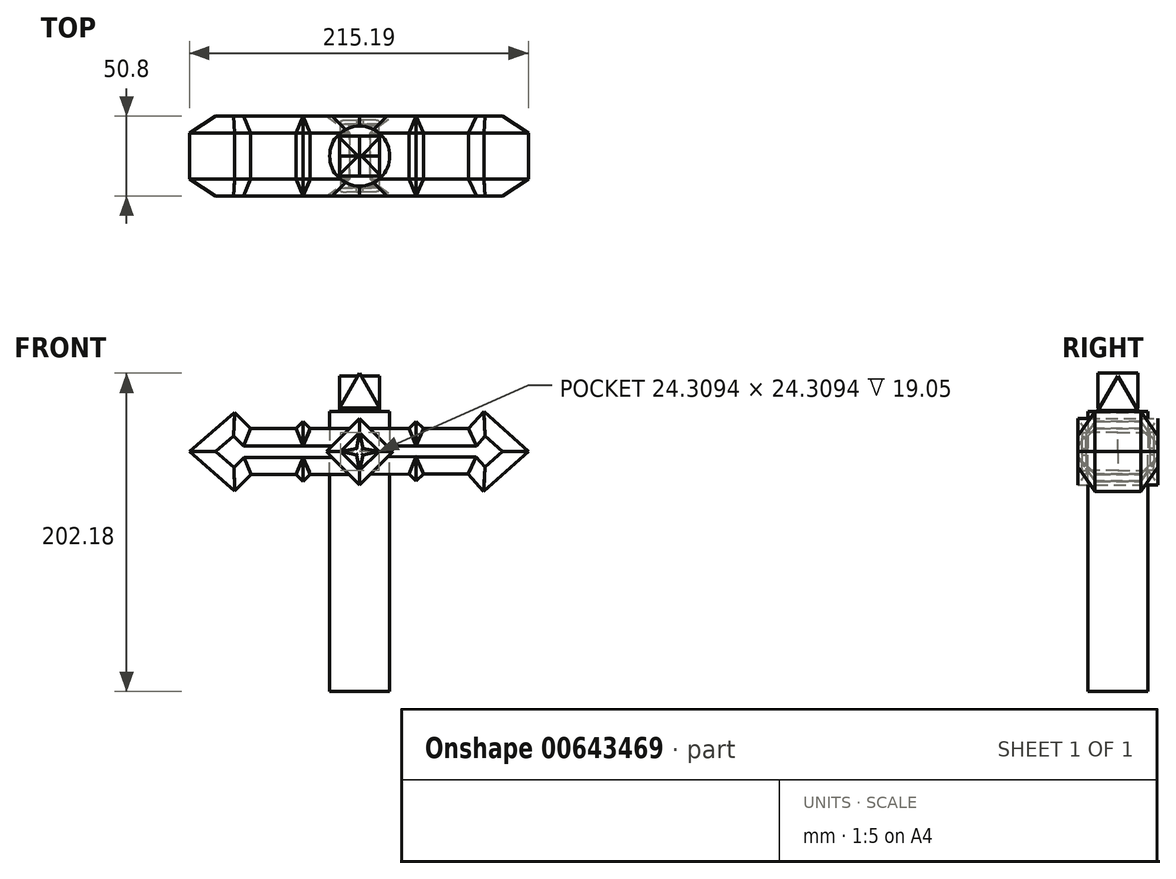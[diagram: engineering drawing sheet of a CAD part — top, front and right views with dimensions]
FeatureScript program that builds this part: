
annotation { "Feature Type Name" : "Feature", "Feature Type Description" : "" }
export const myFeature = defineFeature(function(context is Context, id is Id, definition is map)
    precondition{}
    {
        {
            var Q0;
            Q0=qCreatedBy(makeId("Front.planeOp"),FACE);
            var sketch = newSketch(context, id + "F0", { "sketchPlane" : qUnion([Q0])});
            skLineSegment(sketch, "E0", {"start": v(-21.13, 0) * mm, "end": v(0, 21.13) * mm});
            skLineSegment(sketch, "E1", {"start": v(0, 21.13) * mm, "end": v(21.13, 0) * mm});
            skLineSegment(sketch, "E2", {"start": v(21.13, 0) * mm, "end": v(0, -21.13) * mm});
            skLineSegment(sketch, "E3", {"start": v(0, -21.13) * mm, "end": v(-21.13, 0) * mm});
            skLineSegment(sketch, "E4", {"start": v(-6.56, 14.57) * mm, "end": v(-31.36, 14.57) * mm});
            skLineSegment(sketch, "E5", {"start": v(-31.36, 14.57) * mm, "end": v(-35.9, 19.12) * mm});
            skLineSegment(sketch, "E6", {"start": v(-35.9, 19.12) * mm, "end": v(-40.45, 14.57) * mm});
            skLineSegment(sketch, "E7", {"start": v(-40.45, 14.57) * mm, "end": v(-69.24, 14.57) * mm});
            skLineSegment(sketch, "E8", {"start": v(-69.24, 14.57) * mm, "end": v(-79.35, 24.94) * mm});
            skLineSegment(sketch, "E9", {"start": v(-79.35, 24.94) * mm, "end": v(-108.04, 0) * mm});
            skLineSegment(sketch, "E10", {"start": v(-6.56, -14.57) * mm, "end": v(-31.36, -14.57) * mm});
            skLineSegment(sketch, "E11", {"start": v(-31.36, -14.57) * mm, "end": v(-35.9, -19.12) * mm});
            skLineSegment(sketch, "E12", {"start": v(-35.9, -19.12) * mm, "end": v(-40.45, -14.57) * mm});
            skLineSegment(sketch, "E13", {"start": v(-40.45, -14.57) * mm, "end": v(-68.98, -14.57) * mm});
            skLineSegment(sketch, "E14", {"start": v(-68.98, -14.57) * mm, "end": v(-79.35, -24.94) * mm});
            skLineSegment(sketch, "E15", {"start": v(-79.35, -24.94) * mm, "end": v(-108.04, 0) * mm});
            skLineSegment(sketch, "E16", {"start": v(6.56, 14.57) * mm, "end": v(31.35, 14.57) * mm});
            skLineSegment(sketch, "E17", {"start": v(31.35, 14.57) * mm, "end": v(35.9, 19.11) * mm});
            skLineSegment(sketch, "E18", {"start": v(35.9, 19.11) * mm, "end": v(40.44, 14.57) * mm});
            skLineSegment(sketch, "E19", {"start": v(40.44, 14.57) * mm, "end": v(69.23, 14.57) * mm});
            skLineSegment(sketch, "E20", {"start": v(69.23, 14.57) * mm, "end": v(78.85, 25.4) * mm});
            skLineSegment(sketch, "E21", {"start": v(78.85, 25.4) * mm, "end": v(107.15, 0) * mm});
            skLineSegment(sketch, "E22", {"start": v(107.15, 0) * mm, "end": v(78.7, -25.22) * mm});
            skLineSegment(sketch, "E23", {"start": v(78.7, -25.22) * mm, "end": v(68.97, -14.24) * mm});
            skLineSegment(sketch, "E24", {"start": v(68.97, -14.24) * mm, "end": v(40.44, -14.24) * mm});
            skLineSegment(sketch, "E25", {"start": v(40.44, -14.24) * mm, "end": v(35.9, -18.79) * mm});
            skLineSegment(sketch, "E26", {"start": v(35.9, -18.79) * mm, "end": v(31.35, -14.24) * mm});
            skLineSegment(sketch, "E27", {"start": v(31.35, -14.24) * mm, "end": v(6.56, -14.57) * mm});
            skLineSegment(sketch, "E28.0", {"start": v(0, 12.15) * mm, "end": v(12.15, 0) * mm});
            skLineSegment(sketch, "E28.1", {"start": v(-12.15, 0) * mm, "end": v(0, 12.15) * mm});
            skLineSegment(sketch, "E28.2", {"start": v(0, -12.15) * mm, "end": v(-12.15, 0) * mm});
            skLineSegment(sketch, "E28.3", {"start": v(12.15, 0) * mm, "end": v(0, -12.15) * mm});
            skLineSegment(sketch, "E29", {"start": v(0, 12.15) * mm, "end": v(-2.1, 2.07) * mm});
            skLineSegment(sketch, "E30", {"start": v(-2.1, 2.07) * mm, "end": v(-12.15, 0) * mm});
            skLineSegment(sketch, "E31", {"start": v(-12.15, 0) * mm, "end": v(-2.1, -2.1) * mm});
            skLineSegment(sketch, "E32", {"start": v(-2.1, -2.1) * mm, "end": v(0, -12.15) * mm});
            skLineSegment(sketch, "E33", {"start": v(1.98, -2.1) * mm, "end": v(0, -12.15) * mm});
            skLineSegment(sketch, "E34", {"start": v(12.15, 0) * mm, "end": v(1.98, -2.1) * mm});
            skLineSegment(sketch, "E35", {"start": v(12.15, 0) * mm, "end": v(1.98, 2) * mm});
            skLineSegment(sketch, "E36", {"start": v(1.98, 2) * mm, "end": v(0, 12.15) * mm});
            skLineSegment(sketch, "E37", {"start": v(31.35, 14.57) * mm, "end": v(31.35, -14.24) * mm});
            skLineSegment(sketch, "E38", {"start": v(40.44, 14.57) * mm, "end": v(40.44, -14.24) * mm});
            skLineSegment(sketch, "E39", {"start": v(-31.36, 14.57) * mm, "end": v(-31.36, -14.57) * mm});
            skLineSegment(sketch, "E40", {"start": v(-40.45, -14.57) * mm, "end": v(-40.45, 14.57) * mm});
            skLineSegment(sketch, "E41", {"start": v(78.85, 25.4) * mm, "end": v(78.7, -25.22) * mm});
            skLineSegment(sketch, "E42", {"start": v(-79.35, 24.94) * mm, "end": v(-79.35, -24.94) * mm});
            skLineSegment(sketch, "E43", {"start": v(69.23, 14.57) * mm, "end": v(68.97, -14.24) * mm});
            skLineSegment(sketch, "E44", {"start": v(-69.24, 14.57) * mm, "end": v(-68.98, -14.57) * mm});
            skLineSegment(sketch, "E45", {"start": v(107.15, 0) * mm, "end": v(78.7, 0) * mm});
            skLineSegment(sketch, "E46", {"start": v(-108.04, 0) * mm, "end": v(-79.35, 0) * mm});
            skLineSegment(sketch, "E47", {"start": v(-79.35, 0) * mm, "end": v(-21.13, 0) * mm});
            skLineSegment(sketch, "E48", {"start": v(78.7, 0) * mm, "end": v(21.13, 0) * mm});
            skSolve(sketch);
        }
        {
            var Q0;
            {var subQ0=sQuery(id+"F0.wireOp",EDGE,"E15");Q0=makeQuery(id+"F0.imprint","IMPRINT",FACE,{"disambiguationData":[TD([[makeQuery(id+"F0.imprint","IMPRINT",EDGE,{"derivedFrom":subQ0}),-1.0]])]});}
            var Q1;
            {var subQ0=sQuery(id+"F0.wireOp",EDGE,"E9");Q1=makeQuery(id+"F0.imprint","IMPRINT",FACE,{"disambiguationData":[TD([[makeQuery(id+"F0.imprint","IMPRINT",EDGE,{"derivedFrom":subQ0}),1.0]])]});}
            var Q2;
            {var subQ0=sQuery(id+"F0.wireOp",EDGE,"E8");Q2=makeQuery(id+"F0.imprint","IMPRINT",FACE,{"disambiguationData":[TD([[makeQuery(id+"F0.imprint","IMPRINT",EDGE,{"derivedFrom":subQ0}),1.0]])]});}
            var Q3;
            {var subQ0=sQuery(id+"F0.wireOp",EDGE,"E14");Q3=makeQuery(id+"F0.imprint","IMPRINT",FACE,{"disambiguationData":[TD([[makeQuery(id+"F0.imprint","IMPRINT",EDGE,{"derivedFrom":subQ0}),-1.0]])]});}
            var Q4;
            {var subQ0=sQuery(id+"F0.wireOp",EDGE,"E13");Q4=makeQuery(id+"F0.imprint","IMPRINT",FACE,{"disambiguationData":[TD([[makeQuery(id+"F0.imprint","IMPRINT",EDGE,{"derivedFrom":subQ0}),-1.0]])]});}
            var Q5;
            {var subQ0=sQuery(id+"F0.wireOp",EDGE,"E7");Q5=makeQuery(id+"F0.imprint","IMPRINT",FACE,{"disambiguationData":[TD([[makeQuery(id+"F0.imprint","IMPRINT",EDGE,{"derivedFrom":subQ0}),1.0]])]});}
            var Q6;
            {var subQ5=sQuery(id+"F0.wireOp",EDGE,"E5");Q6=makeQuery(id+"F0.imprint","IMPRINT",FACE,{"disambiguationData":[TD([[makeQuery(id+"F0.imprint","IMPRINT",EDGE,{"derivedFrom":subQ5}),1.0]])]});}
            var Q7;
            {var subQ1=sQuery(id+"F0.wireOp",EDGE,"E11");Q7=makeQuery(id+"F0.imprint","IMPRINT",FACE,{"disambiguationData":[TD([[makeQuery(id+"F0.imprint","IMPRINT",EDGE,{"derivedFrom":subQ1}),-1.0]])]});}
            extrude(context, id + "F1", {"entities" : qUnion([Q0, Q1, Q2, Q3, Q4, Q5, Q6, Q7]), "depth" : 25.4 * mm, "offsetDistance" : 25.4 * mm});
        }
        {
            var Q0;
            {var subQ3=sQuery(id+"F0.wireOp",EDGE,"E4");Q0=makeQuery(id+"F0.imprint","IMPRINT",FACE,{"disambiguationData":[TD([[makeQuery(id+"F0.imprint","IMPRINT",EDGE,{"derivedFrom":subQ3}),1.0]])]});}
            var Q1;
            {var subQ3=sQuery(id+"F0.wireOp",EDGE,"E10");Q1=makeQuery(id+"F0.imprint","IMPRINT",FACE,{"disambiguationData":[TD([[makeQuery(id+"F0.imprint","IMPRINT",EDGE,{"derivedFrom":subQ3}),-1.0]])]});}
            var Q2;
            Q2=makeQuery(id+"F0.imprint","IMPRINT",FACE,{"disambiguationData":[TD([[makeQuery(id+"F0.imprint","IMPRINT",EDGE,{"derivedFrom":sQuery(id+"F0.wireOp",EDGE,"E28.0")}),1.0]])]});
            var Q3;
            {var subQ3=sQuery(id+"F0.wireOp",EDGE,"E27");Q3=makeQuery(id+"F0.imprint","IMPRINT",FACE,{"disambiguationData":[TD([[makeQuery(id+"F0.imprint","IMPRINT",EDGE,{"derivedFrom":subQ3}),-1.0]])]});}
            var Q4;
            {var subQ3=sQuery(id+"F0.wireOp",EDGE,"E16");Q4=makeQuery(id+"F0.imprint","IMPRINT",FACE,{"disambiguationData":[TD([[makeQuery(id+"F0.imprint","IMPRINT",EDGE,{"derivedFrom":subQ3}),-1.0]])]});}
            var Q5;
            {var subQ1=sQuery(id+"F0.wireOp",EDGE,"E17");Q5=makeQuery(id+"F0.imprint","IMPRINT",FACE,{"disambiguationData":[TD([[makeQuery(id+"F0.imprint","IMPRINT",EDGE,{"derivedFrom":subQ1}),-1.0]])]});}
            var Q6;
            {var subQ0=sQuery(id+"F0.wireOp",EDGE,"E19");Q6=makeQuery(id+"F0.imprint","IMPRINT",FACE,{"disambiguationData":[TD([[makeQuery(id+"F0.imprint","IMPRINT",EDGE,{"derivedFrom":subQ0}),-1.0]])]});}
            var Q7;
            {var subQ1=sQuery(id+"F0.wireOp",EDGE,"E25");Q7=makeQuery(id+"F0.imprint","IMPRINT",FACE,{"disambiguationData":[TD([[makeQuery(id+"F0.imprint","IMPRINT",EDGE,{"derivedFrom":subQ1}),-1.0]])]});}
            var Q8;
            {var subQ0=sQuery(id+"F0.wireOp",EDGE,"E24");Q8=makeQuery(id+"F0.imprint","IMPRINT",FACE,{"disambiguationData":[TD([[makeQuery(id+"F0.imprint","IMPRINT",EDGE,{"derivedFrom":subQ0}),-1.0]])]});}
            var Q9;
            {var subQ5=sQuery(id+"F0.wireOp",EDGE,"E23");Q9=makeQuery(id+"F0.imprint","IMPRINT",FACE,{"disambiguationData":[TD([[makeQuery(id+"F0.imprint","IMPRINT",EDGE,{"derivedFrom":subQ5}),-1.0]])]});}
            var Q10;
            {var subQ6=sQuery(id+"F0.wireOp",EDGE,"E20");Q10=makeQuery(id+"F0.imprint","IMPRINT",FACE,{"disambiguationData":[TD([[makeQuery(id+"F0.imprint","IMPRINT",EDGE,{"derivedFrom":subQ6}),-1.0]])]});}
            var Q11;
            {var subQ0=sQuery(id+"F0.wireOp",EDGE,"E21");Q11=makeQuery(id+"F0.imprint","IMPRINT",FACE,{"disambiguationData":[TD([[makeQuery(id+"F0.imprint","IMPRINT",EDGE,{"derivedFrom":subQ0}),-1.0]])]});}
            var Q12;
            {var subQ0=sQuery(id+"F0.wireOp",EDGE,"E22");Q12=makeQuery(id+"F0.imprint","IMPRINT",FACE,{"disambiguationData":[TD([[makeQuery(id+"F0.imprint","IMPRINT",EDGE,{"derivedFrom":subQ0}),-1.0]])]});}
            extrude(context, id + "F2", {"entities" : qUnion([Q0, Q1, Q2, Q3, Q4, Q5, Q6, Q7, Q8, Q9, Q10, Q11, Q12]), "operationType" : NewBodyOperationType.ADD, "depth" : 25.4 * mm, "offsetDistance" : 25.4 * mm});
        }
        {
            var Q0;
            Q0=makeQuery(id+"F2.opExtrude","CAP_EDGE",EDGE,{"disambiguationData":[OSD([sQuery(id+"F0.wireOp",EDGE,"E28.1")])],"isStart":false});
            var Q1;
            Q1=makeQuery(id+"F2.opExtrude","CAP_EDGE",EDGE,{"disambiguationData":[OSD([sQuery(id+"F0.wireOp",EDGE,"E28.0")])],"isStart":false});
            var Q2;
            Q2=makeQuery(id+"F2.opExtrude","CAP_EDGE",EDGE,{"disambiguationData":[OSD([sQuery(id+"F0.wireOp",EDGE,"E28.3")])],"isStart":false});
            var Q3;
            Q3=makeQuery(id+"F2.opExtrude","CAP_EDGE",EDGE,{"disambiguationData":[OSD([sQuery(id+"F0.wireOp",EDGE,"E28.2")])],"isStart":false});
            chamfer(context, id + "F3", {"entities" : qUnion([Q0, Q1, Q2, Q3]), "width" : 6.35 * mm, "tangentPropagation" : true});
        }
        {
            var Q0;
            Q0=makeQuery(id+"F0.imprint","IMPRINT",FACE,{"disambiguationData":[TD([[makeQuery(id+"F0.imprint","IMPRINT",EDGE,{"derivedFrom":sQuery(id+"F0.wireOp",EDGE,"E29")}),1.0]])]});
            extrude(context, id + "F4", {"entities" : qUnion([Q0]), "depth" : 22.86 * mm, "offsetDistance" : 25.4 * mm});
        }
        {
            var Q0;
            Q0=makeQuery(id+"F0.imprint","IMPRINT",FACE,{"disambiguationData":[TD([[makeQuery(id+"F0.imprint","IMPRINT",EDGE,{"derivedFrom":sQuery(id+"F0.wireOp",EDGE,"E28.0")}),-1.0]])]});
            var Q1;
            Q1=makeQuery(id+"F0.imprint","IMPRINT",FACE,{"disambiguationData":[TD([[makeQuery(id+"F0.imprint","IMPRINT",EDGE,{"derivedFrom":sQuery(id+"F0.wireOp",EDGE,"E28.3")}),-1.0]])]});
            var Q2;
            Q2=makeQuery(id+"F0.imprint","IMPRINT",FACE,{"disambiguationData":[TD([[makeQuery(id+"F0.imprint","IMPRINT",EDGE,{"derivedFrom":sQuery(id+"F0.wireOp",EDGE,"E28.2")}),-1.0]])]});
            var Q3;
            Q3=makeQuery(id+"F0.imprint","IMPRINT",FACE,{"disambiguationData":[TD([[makeQuery(id+"F0.imprint","IMPRINT",EDGE,{"derivedFrom":sQuery(id+"F0.wireOp",EDGE,"E28.1")}),-1.0]])]});
            extrude(context, id + "F5", {"entities" : qUnion([Q0, Q1, Q2, Q3]), "depth" : 20.32 * mm, "offsetDistance" : 25.4 * mm});
        }
        {
            var Q0;
            Q0=makeQuery(id+"F4.opExtrude","CAP_EDGE",EDGE,{"disambiguationData":[OSD([sQuery(id+"F0.wireOp",EDGE,"E35")])],"isStart":false});
            var Q1;
            Q1=makeQuery(id+"F4.opExtrude","CAP_EDGE",EDGE,{"disambiguationData":[OSD([sQuery(id+"F0.wireOp",EDGE,"E34")])],"isStart":false});
            var Q2;
            Q2=makeQuery(id+"F4.opExtrude","CAP_EDGE",EDGE,{"disambiguationData":[OSD([sQuery(id+"F0.wireOp",EDGE,"E33")])],"isStart":false});
            var Q3;
            Q3=makeQuery(id+"F4.opExtrude","CAP_EDGE",EDGE,{"disambiguationData":[OSD([sQuery(id+"F0.wireOp",EDGE,"E32")])],"isStart":false});
            var Q4;
            Q4=makeQuery(id+"F4.opExtrude","CAP_EDGE",EDGE,{"disambiguationData":[OSD([sQuery(id+"F0.wireOp",EDGE,"E31")])],"isStart":false});
            var Q5;
            Q5=makeQuery(id+"F4.opExtrude","CAP_EDGE",EDGE,{"disambiguationData":[OSD([sQuery(id+"F0.wireOp",EDGE,"E30")])],"isStart":false});
            var Q6;
            Q6=makeQuery(id+"F4.opExtrude","CAP_EDGE",EDGE,{"disambiguationData":[OSD([sQuery(id+"F0.wireOp",EDGE,"E29")])],"isStart":false});
            var Q7;
            Q7=makeQuery(id+"F4.opExtrude","CAP_EDGE",EDGE,{"disambiguationData":[OSD([sQuery(id+"F0.wireOp",EDGE,"E36")])],"isStart":false});
            fillet(context, id + "F6", {"entities" : qUnion([Q0, Q1, Q2, Q3, Q4, Q5, Q6, Q7]), "radius" : 0.76 * mm, "tangentPropagation" : true, "allowEdgeOverflow" : false});
        }
        {
            var Q0;
            Q0=makeQuery(id+"F2.opExtrude","CAP_EDGE",EDGE,{"disambiguationData":[OSD([sQuery(id+"F0.wireOp",EDGE,"E20")])],"isStart":false});
            var Q1;
            Q1=makeQuery(id+"F2.opExtrude","CAP_EDGE",EDGE,{"disambiguationData":[OSD([sQuery(id+"F0.wireOp",EDGE,"E21")])],"isStart":false});
            var Q2;
            Q2=makeQuery(id+"F2.opExtrude","CAP_EDGE",EDGE,{"disambiguationData":[OSD([sQuery(id+"F0.wireOp",EDGE,"E22")])],"isStart":false});
            var Q3;
            Q3=makeQuery(id+"F2.opExtrude","CAP_EDGE",EDGE,{"disambiguationData":[OSD([sQuery(id+"F0.wireOp",EDGE,"E23")])],"isStart":false});
            var Q4;
            Q4=makeQuery(id+"F2.opExtrude","CAP_EDGE",EDGE,{"disambiguationData":[OSD([sQuery(id+"F0.wireOp",EDGE,"E24")])],"isStart":false});
            var Q5;
            Q5=makeQuery(id+"F2.opExtrude","CAP_EDGE",EDGE,{"disambiguationData":[OSD([sQuery(id+"F0.wireOp",EDGE,"E19")])],"isStart":false});
            var Q6;
            Q6=makeQuery(id+"F2.opExtrude","CAP_EDGE",EDGE,{"disambiguationData":[OSD([sQuery(id+"F0.wireOp",EDGE,"E25")])],"isStart":false});
            var Q7;
            Q7=makeQuery(id+"F2.opExtrude","CAP_EDGE",EDGE,{"disambiguationData":[OSD([sQuery(id+"F0.wireOp",EDGE,"E26")])],"isStart":false});
            var Q8;
            Q8=makeQuery(id+"F2.opExtrude","CAP_EDGE",EDGE,{"disambiguationData":[OSD([sQuery(id+"F0.wireOp",EDGE,"E18")])],"isStart":false});
            var Q9;
            Q9=makeQuery(id+"F2.opExtrude","CAP_EDGE",EDGE,{"disambiguationData":[OSD([sQuery(id+"F0.wireOp",EDGE,"E17")])],"isStart":false});
            var Q10;
            Q10=makeQuery(id+"F2.opExtrude","CAP_EDGE",EDGE,{"disambiguationData":[OSD([sQuery(id+"F0.wireOp",EDGE,"E27")])],"isStart":false});
            var Q11;
            Q11=makeQuery(id+"F2.opExtrude","CAP_EDGE",EDGE,{"disambiguationData":[OSD([sQuery(id+"F0.wireOp",EDGE,"E16")])],"isStart":false});
            var Q12;
            Q12=makeQuery(id+"F2.opExtrude","CAP_EDGE",EDGE,{"disambiguationData":[OSD([sQuery(id+"F0.wireOp",EDGE,"E10")])],"isStart":false});
            var Q13;
            Q13=makeQuery(id+"F1.opExtrude","CAP_EDGE",EDGE,{"disambiguationData":[OSD([sQuery(id+"F0.wireOp",EDGE,"E11")])],"isStart":false});
            var Q14;
            Q14=makeQuery(id+"F1.opExtrude","CAP_EDGE",EDGE,{"disambiguationData":[OSD([sQuery(id+"F0.wireOp",EDGE,"E13")])],"isStart":false});
            var Q15;
            Q15=makeQuery(id+"F1.opExtrude","CAP_EDGE",EDGE,{"disambiguationData":[OSD([sQuery(id+"F0.wireOp",EDGE,"E14")])],"isStart":false});
            var Q16;
            Q16=makeQuery(id+"F1.opExtrude","CAP_EDGE",EDGE,{"disambiguationData":[OSD([sQuery(id+"F0.wireOp",EDGE,"E15")])],"isStart":false});
            var Q17;
            Q17=makeQuery(id+"F1.opExtrude","CAP_EDGE",EDGE,{"disambiguationData":[OSD([sQuery(id+"F0.wireOp",EDGE,"E12")])],"isStart":false});
            var Q18;
            Q18=makeQuery(id+"F2.opExtrude","CAP_EDGE",EDGE,{"disambiguationData":[OSD([sQuery(id+"F0.wireOp",EDGE,"E4")])],"isStart":false});
            var Q19;
            Q19=makeQuery(id+"F1.opExtrude","CAP_EDGE",EDGE,{"disambiguationData":[OSD([sQuery(id+"F0.wireOp",EDGE,"E5")])],"isStart":false});
            var Q20;
            Q20=makeQuery(id+"F1.opExtrude","CAP_EDGE",EDGE,{"disambiguationData":[OSD([sQuery(id+"F0.wireOp",EDGE,"E6")])],"isStart":false});
            var Q21;
            Q21=makeQuery(id+"F1.opExtrude","CAP_EDGE",EDGE,{"disambiguationData":[OSD([sQuery(id+"F0.wireOp",EDGE,"E7")])],"isStart":false});
            var Q22;
            Q22=makeQuery(id+"F1.opExtrude","CAP_EDGE",EDGE,{"disambiguationData":[OSD([sQuery(id+"F0.wireOp",EDGE,"E8")])],"isStart":false});
            var Q23;
            Q23=makeQuery(id+"F1.opExtrude","CAP_EDGE",EDGE,{"disambiguationData":[OSD([sQuery(id+"F0.wireOp",EDGE,"E9")])],"isStart":false});
            chamfer(context, id + "F7", {"entities" : qUnion([Q0, Q1, Q2, Q3, Q4, Q5, Q6, Q7, Q8, Q9, Q10, Q11, Q12, Q13, Q14, Q15, Q16, Q17, Q18, Q19, Q20, Q21, Q22, Q23]), "width" : 10.92 * mm, "tangentPropagation" : true});
        }
        {
            var Q0;
            Q0=makeQuery(id+"F1.opExtrude","SWEPT_BODY",BODY,{"disambiguationData":[OSD([sQuery(id+"F0.wireOp",EDGE,"E5"),sQuery(id+"F0.wireOp",EDGE,"E6"),sQuery(id+"F0.wireOp",EDGE,"E7"),sQuery(id+"F0.wireOp",EDGE,"E8"),sQuery(id+"F0.wireOp",EDGE,"E9"),sQuery(id+"F0.wireOp",EDGE,"E11"),sQuery(id+"F0.wireOp",EDGE,"E12"),sQuery(id+"F0.wireOp",EDGE,"E13"),sQuery(id+"F0.wireOp",EDGE,"E14"),sQuery(id+"F0.wireOp",EDGE,"E15"),sQuery(id+"F0.wireOp",EDGE,"E39")])]});
            var Q1;
            Q1=qCreatedBy(makeId("Front.planeOp"),FACE);
            mirror(context, id + "F8", {"operationType" : NewBodyOperationType.ADD, "entities" : qUnion([Q0]), "mirrorPlane" : qUnion([Q1])});
        }
        {
            var Q0;
            Q0=makeQuery(id+"F4.opExtrude","SWEPT_BODY",BODY,{"disambiguationData":[OSD([sQuery(id+"F0.wireOp",EDGE,"E29"),sQuery(id+"F0.wireOp",EDGE,"E30"),sQuery(id+"F0.wireOp",EDGE,"E31"),sQuery(id+"F0.wireOp",EDGE,"E32"),sQuery(id+"F0.wireOp",EDGE,"E33"),sQuery(id+"F0.wireOp",EDGE,"E34"),sQuery(id+"F0.wireOp",EDGE,"E35"),sQuery(id+"F0.wireOp",EDGE,"E36")])]});
            var Q1;
            Q1=makeQuery(id+"F5.opExtrude","SWEPT_BODY",BODY,{"disambiguationData":[OSD([sQuery(id+"F0.wireOp",EDGE,"E28.0"),sQuery(id+"F0.wireOp",EDGE,"E35"),sQuery(id+"F0.wireOp",EDGE,"E36")])]});
            var Q2;
            Q2=makeQuery(id+"F5.opExtrude","SWEPT_BODY",BODY,{"disambiguationData":[OSD([sQuery(id+"F0.wireOp",EDGE,"E28.1"),sQuery(id+"F0.wireOp",EDGE,"E29"),sQuery(id+"F0.wireOp",EDGE,"E30")])]});
            var Q3;
            Q3=makeQuery(id+"F5.opExtrude","SWEPT_BODY",BODY,{"disambiguationData":[OSD([sQuery(id+"F0.wireOp",EDGE,"E28.2"),sQuery(id+"F0.wireOp",EDGE,"E31"),sQuery(id+"F0.wireOp",EDGE,"E32")])]});
            var Q4;
            Q4=makeQuery(id+"F5.opExtrude","SWEPT_BODY",BODY,{"disambiguationData":[OSD([sQuery(id+"F0.wireOp",EDGE,"E28.3"),sQuery(id+"F0.wireOp",EDGE,"E33"),sQuery(id+"F0.wireOp",EDGE,"E34")])]});
            var Q5;
            Q5=qCreatedBy(makeId("Front.planeOp"),FACE);
            mirror(context, id + "F9", {"entities" : qUnion([Q0, Q1, Q2, Q3, Q4]), "mirrorPlane" : qUnion([Q5])});
        }
        {
            var Q0;
            Q0=qCreatedBy(makeId("Top.planeOp"),FACE);
            var sketch = newSketch(context, id + "F10", { "sketchPlane" : qUnion([Q0])});
            skCircle(sketch, "E49", {"center": v(0, 0) * mm, "radius": 19.05 * mm});
            skSolve(sketch);
        }
        {
            var Q0;
            Q0=makeQuery(id+"F10.imprint","IMPRINT",FACE,{"disambiguationData":[TD([[makeQuery(id+"F10.imprint","IMPRINT",EDGE,{"derivedFrom":sQuery(id+"F10.wireOp",EDGE,"E49")}),1.0]])]});
            extrude(context, id + "F11", {"entities" : qUnion([Q0]), "oppositeDirection" : true, "depth" : 152.4 * mm, "offsetDistance" : 25.4 * mm});
        }
        {
            var Q0;
            Q0=qCreatedBy(makeId("Top.planeOp"),FACE);
            var sketch = newSketch(context, id + "F12", { "sketchPlane" : qUnion([Q0])});
            skCircle(sketch, "E50", {"center": v(0, 0) * mm, "radius": 19.05 * mm});
            skSolve(sketch);
        }
        {
            var Q0;
            Q0 = qSketchRegion(id + "F12", true);
            extrude(context, id + "F13", {"entities" : qUnion([Q0]), "depth" : 25.4 * mm, "offsetDistance" : 25.4 * mm});
        }
        {
            var Q0;
            {var subQ0=sQuery(id+"F0.wireOp",EDGE,"E21");Q0=makeQuery(id+"F7.opChamfer","BLEND_EDGE",EDGE,{"blendedFrom":[makeQuery(id+"F2.opExtrude","CAP_EDGE",EDGE,{"disambiguationData":[OSD([subQ0])],"isStart":false}),makeQuery(id+"F2.opExtrude","SWEPT_FACE",FACE,{"disambiguationData":[OSD([subQ0])]})],"blendedInto":[makeQuery(id+"F2.opExtrude","SWEPT_FACE",FACE,{"disambiguationData":[OSD([subQ0])]})]});}
            var Q1;
            {var subQ0=sQuery(id+"F0.wireOp",EDGE,"E22");Q1=makeQuery(id+"F7.opChamfer","BLEND_EDGE",EDGE,{"blendedFrom":[makeQuery(id+"F2.opExtrude","CAP_EDGE",EDGE,{"disambiguationData":[OSD([subQ0])],"isStart":false}),makeQuery(id+"F2.opExtrude","SWEPT_FACE",FACE,{"disambiguationData":[OSD([subQ0])]})],"blendedInto":[makeQuery(id+"F2.opExtrude","SWEPT_FACE",FACE,{"disambiguationData":[OSD([subQ0])]})]});}
            var Q2;
            {var subQ0=sQuery(id+"F0.wireOp",EDGE,"E20");Q2=makeQuery(id+"F7.opChamfer","BLEND_EDGE",EDGE,{"blendedFrom":[makeQuery(id+"F2.opExtrude","CAP_EDGE",EDGE,{"disambiguationData":[OSD([subQ0])],"isStart":false}),makeQuery(id+"F2.opExtrude","SWEPT_FACE",FACE,{"disambiguationData":[OSD([subQ0])]})],"blendedInto":[makeQuery(id+"F2.opExtrude","SWEPT_FACE",FACE,{"disambiguationData":[OSD([subQ0])]})]});}
            var Q3;
            {var subQ0=sQuery(id+"F0.wireOp",EDGE,"E19");Q3=makeQuery(id+"F7.opChamfer","BLEND_EDGE",EDGE,{"blendedFrom":[makeQuery(id+"F2.opExtrude","CAP_EDGE",EDGE,{"disambiguationData":[OSD([subQ0])],"isStart":false}),makeQuery(id+"F2.opExtrude","SWEPT_FACE",FACE,{"disambiguationData":[OSD([subQ0])]})],"blendedInto":[makeQuery(id+"F2.opExtrude","SWEPT_FACE",FACE,{"disambiguationData":[OSD([subQ0])]})]});}
            var Q4;
            {var subQ0=sQuery(id+"F0.wireOp",EDGE,"E24");Q4=makeQuery(id+"F7.opChamfer","BLEND_EDGE",EDGE,{"blendedFrom":[makeQuery(id+"F2.opExtrude","CAP_EDGE",EDGE,{"disambiguationData":[OSD([subQ0])],"isStart":false}),makeQuery(id+"F2.opExtrude","SWEPT_FACE",FACE,{"disambiguationData":[OSD([subQ0])]})],"blendedInto":[makeQuery(id+"F2.opExtrude","SWEPT_FACE",FACE,{"disambiguationData":[OSD([subQ0])]})]});}
            var Q5;
            {var subQ0=sQuery(id+"F0.wireOp",EDGE,"E23");Q5=makeQuery(id+"F7.opChamfer","BLEND_EDGE",EDGE,{"blendedFrom":[makeQuery(id+"F2.opExtrude","CAP_EDGE",EDGE,{"disambiguationData":[OSD([subQ0])],"isStart":false}),makeQuery(id+"F2.opExtrude","SWEPT_FACE",FACE,{"disambiguationData":[OSD([subQ0])]})],"blendedInto":[makeQuery(id+"F2.opExtrude","SWEPT_FACE",FACE,{"disambiguationData":[OSD([subQ0])]})]});}
            var Q6;
            {var subQ0=sQuery(id+"F0.wireOp",EDGE,"E25");Q6=makeQuery(id+"F7.opChamfer","BLEND_EDGE",EDGE,{"blendedFrom":[makeQuery(id+"F2.opExtrude","CAP_EDGE",EDGE,{"disambiguationData":[OSD([subQ0])],"isStart":false}),makeQuery(id+"F2.opExtrude","SWEPT_FACE",FACE,{"disambiguationData":[OSD([subQ0])]})],"blendedInto":[makeQuery(id+"F2.opExtrude","SWEPT_FACE",FACE,{"disambiguationData":[OSD([subQ0])]})]});}
            var Q7;
            {var subQ0=sQuery(id+"F0.wireOp",EDGE,"E27");Q7=makeQuery(id+"F7.opChamfer","BLEND_EDGE",EDGE,{"blendedFrom":[makeQuery(id+"F2.opExtrude","CAP_EDGE",EDGE,{"disambiguationData":[OSD([subQ0])],"isStart":false}),makeQuery(id+"F2.opExtrude","SWEPT_FACE",FACE,{"disambiguationData":[OSD([subQ0])]})],"blendedInto":[makeQuery(id+"F2.opExtrude","SWEPT_FACE",FACE,{"disambiguationData":[OSD([subQ0])]})]});}
            var Q8;
            {var subQ0=sQuery(id+"F0.wireOp",EDGE,"E16");Q8=makeQuery(id+"F7.opChamfer","BLEND_EDGE",EDGE,{"blendedFrom":[makeQuery(id+"F2.opExtrude","CAP_EDGE",EDGE,{"disambiguationData":[OSD([subQ0])],"isStart":false}),makeQuery(id+"F2.opExtrude","SWEPT_FACE",FACE,{"disambiguationData":[OSD([subQ0])]})],"blendedInto":[makeQuery(id+"F2.opExtrude","SWEPT_FACE",FACE,{"disambiguationData":[OSD([subQ0])]})]});}
            var Q9;
            {var subQ0=sQuery(id+"F0.wireOp",EDGE,"E17");Q9=makeQuery(id+"F7.opChamfer","BLEND_EDGE",EDGE,{"blendedFrom":[makeQuery(id+"F2.opExtrude","CAP_EDGE",EDGE,{"disambiguationData":[OSD([subQ0])],"isStart":false}),makeQuery(id+"F2.opExtrude","SWEPT_FACE",FACE,{"disambiguationData":[OSD([subQ0])]})],"blendedInto":[makeQuery(id+"F2.opExtrude","SWEPT_FACE",FACE,{"disambiguationData":[OSD([subQ0])]})]});}
            var Q10;
            {var subQ0=sQuery(id+"F0.wireOp",EDGE,"E26");Q10=makeQuery(id+"F7.opChamfer","BLEND_EDGE",EDGE,{"blendedFrom":[makeQuery(id+"F2.opExtrude","CAP_EDGE",EDGE,{"disambiguationData":[OSD([subQ0])],"isStart":false}),makeQuery(id+"F2.opExtrude","SWEPT_FACE",FACE,{"disambiguationData":[OSD([subQ0])]})],"blendedInto":[makeQuery(id+"F2.opExtrude","SWEPT_FACE",FACE,{"disambiguationData":[OSD([subQ0])]})]});}
            var Q11;
            {var subQ0=sQuery(id+"F0.wireOp",EDGE,"E18");Q11=makeQuery(id+"F7.opChamfer","BLEND_EDGE",EDGE,{"blendedFrom":[makeQuery(id+"F2.opExtrude","CAP_EDGE",EDGE,{"disambiguationData":[OSD([subQ0])],"isStart":false}),makeQuery(id+"F2.opExtrude","SWEPT_FACE",FACE,{"disambiguationData":[OSD([subQ0])]})],"blendedInto":[makeQuery(id+"F2.opExtrude","SWEPT_FACE",FACE,{"disambiguationData":[OSD([subQ0])]})]});}
            var Q12;
            {var subQ0=sQuery(id+"F0.wireOp",EDGE,"E10");Q12=makeQuery(id+"F7.opChamfer","BLEND_EDGE",EDGE,{"blendedFrom":[makeQuery(id+"F2.opExtrude","CAP_EDGE",EDGE,{"disambiguationData":[OSD([subQ0])],"isStart":false}),makeQuery(id+"F2.opExtrude","SWEPT_FACE",FACE,{"disambiguationData":[OSD([subQ0])]})],"blendedInto":[makeQuery(id+"F2.opExtrude","SWEPT_FACE",FACE,{"disambiguationData":[OSD([subQ0])]})]});}
            var Q13;
            {var subQ0=sQuery(id+"F0.wireOp",EDGE,"E4");Q13=makeQuery(id+"F7.opChamfer","BLEND_EDGE",EDGE,{"blendedFrom":[makeQuery(id+"F2.opExtrude","CAP_EDGE",EDGE,{"disambiguationData":[OSD([subQ0])],"isStart":false}),makeQuery(id+"F2.opExtrude","SWEPT_FACE",FACE,{"disambiguationData":[OSD([subQ0])]})],"blendedInto":[makeQuery(id+"F2.opExtrude","SWEPT_FACE",FACE,{"disambiguationData":[OSD([subQ0])]})]});}
            var Q14;
            {var subQ0=sQuery(id+"F0.wireOp",EDGE,"E5");Q14=makeQuery(id+"F7.opChamfer","BLEND_EDGE",EDGE,{"blendedFrom":[makeQuery(id+"F1.opExtrude","CAP_EDGE",EDGE,{"disambiguationData":[OSD([subQ0])],"isStart":false}),makeQuery(id+"F1.opExtrude","SWEPT_FACE",FACE,{"disambiguationData":[OSD([subQ0])]})],"blendedInto":[makeQuery(id+"F1.opExtrude","SWEPT_FACE",FACE,{"disambiguationData":[OSD([subQ0])]})]});}
            var Q15;
            {var subQ0=sQuery(id+"F0.wireOp",EDGE,"E6");Q15=makeQuery(id+"F7.opChamfer","BLEND_EDGE",EDGE,{"blendedFrom":[makeQuery(id+"F1.opExtrude","CAP_EDGE",EDGE,{"disambiguationData":[OSD([subQ0])],"isStart":false}),makeQuery(id+"F1.opExtrude","SWEPT_FACE",FACE,{"disambiguationData":[OSD([subQ0])]})],"blendedInto":[makeQuery(id+"F1.opExtrude","SWEPT_FACE",FACE,{"disambiguationData":[OSD([subQ0])]})]});}
            var Q16;
            {var subQ0=sQuery(id+"F0.wireOp",EDGE,"E11");Q16=makeQuery(id+"F7.opChamfer","BLEND_EDGE",EDGE,{"blendedFrom":[makeQuery(id+"F1.opExtrude","CAP_EDGE",EDGE,{"disambiguationData":[OSD([subQ0])],"isStart":false}),makeQuery(id+"F1.opExtrude","SWEPT_FACE",FACE,{"disambiguationData":[OSD([subQ0])]})],"blendedInto":[makeQuery(id+"F1.opExtrude","SWEPT_FACE",FACE,{"disambiguationData":[OSD([subQ0])]})]});}
            var Q17;
            {var subQ0=sQuery(id+"F0.wireOp",EDGE,"E12");Q17=makeQuery(id+"F7.opChamfer","BLEND_EDGE",EDGE,{"blendedFrom":[makeQuery(id+"F1.opExtrude","CAP_EDGE",EDGE,{"disambiguationData":[OSD([subQ0])],"isStart":false}),makeQuery(id+"F1.opExtrude","SWEPT_FACE",FACE,{"disambiguationData":[OSD([subQ0])]})],"blendedInto":[makeQuery(id+"F1.opExtrude","SWEPT_FACE",FACE,{"disambiguationData":[OSD([subQ0])]})]});}
            var Q18;
            {var subQ0=sQuery(id+"F0.wireOp",EDGE,"E13");Q18=makeQuery(id+"F7.opChamfer","BLEND_EDGE",EDGE,{"blendedFrom":[makeQuery(id+"F1.opExtrude","CAP_EDGE",EDGE,{"disambiguationData":[OSD([subQ0])],"isStart":false}),makeQuery(id+"F1.opExtrude","SWEPT_FACE",FACE,{"disambiguationData":[OSD([subQ0])]})],"blendedInto":[makeQuery(id+"F1.opExtrude","SWEPT_FACE",FACE,{"disambiguationData":[OSD([subQ0])]})]});}
            var Q19;
            {var subQ0=sQuery(id+"F0.wireOp",EDGE,"E7");Q19=makeQuery(id+"F7.opChamfer","BLEND_EDGE",EDGE,{"blendedFrom":[makeQuery(id+"F1.opExtrude","CAP_EDGE",EDGE,{"disambiguationData":[OSD([subQ0])],"isStart":false}),makeQuery(id+"F1.opExtrude","SWEPT_FACE",FACE,{"disambiguationData":[OSD([subQ0])]})],"blendedInto":[makeQuery(id+"F1.opExtrude","SWEPT_FACE",FACE,{"disambiguationData":[OSD([subQ0])]})]});}
            var Q20;
            {var subQ0=sQuery(id+"F0.wireOp",EDGE,"E8");Q20=makeQuery(id+"F7.opChamfer","BLEND_EDGE",EDGE,{"blendedFrom":[makeQuery(id+"F1.opExtrude","CAP_EDGE",EDGE,{"disambiguationData":[OSD([subQ0])],"isStart":false}),makeQuery(id+"F1.opExtrude","SWEPT_FACE",FACE,{"disambiguationData":[OSD([subQ0])]})],"blendedInto":[makeQuery(id+"F1.opExtrude","SWEPT_FACE",FACE,{"disambiguationData":[OSD([subQ0])]})]});}
            var Q21;
            {var subQ0=sQuery(id+"F0.wireOp",EDGE,"E14");Q21=makeQuery(id+"F7.opChamfer","BLEND_EDGE",EDGE,{"blendedFrom":[makeQuery(id+"F1.opExtrude","CAP_EDGE",EDGE,{"disambiguationData":[OSD([subQ0])],"isStart":false}),makeQuery(id+"F1.opExtrude","SWEPT_FACE",FACE,{"disambiguationData":[OSD([subQ0])]})],"blendedInto":[makeQuery(id+"F1.opExtrude","SWEPT_FACE",FACE,{"disambiguationData":[OSD([subQ0])]})]});}
            var Q22;
            {var subQ0=sQuery(id+"F0.wireOp",EDGE,"E15");Q22=makeQuery(id+"F7.opChamfer","BLEND_EDGE",EDGE,{"blendedFrom":[makeQuery(id+"F1.opExtrude","CAP_EDGE",EDGE,{"disambiguationData":[OSD([subQ0])],"isStart":false}),makeQuery(id+"F1.opExtrude","SWEPT_FACE",FACE,{"disambiguationData":[OSD([subQ0])]})],"blendedInto":[makeQuery(id+"F1.opExtrude","SWEPT_FACE",FACE,{"disambiguationData":[OSD([subQ0])]})]});}
            var Q23;
            {var subQ0=sQuery(id+"F0.wireOp",EDGE,"E9");Q23=makeQuery(id+"F7.opChamfer","BLEND_EDGE",EDGE,{"blendedFrom":[makeQuery(id+"F1.opExtrude","CAP_EDGE",EDGE,{"disambiguationData":[OSD([subQ0])],"isStart":false}),makeQuery(id+"F1.opExtrude","SWEPT_FACE",FACE,{"disambiguationData":[OSD([subQ0])]})],"blendedInto":[makeQuery(id+"F1.opExtrude","SWEPT_FACE",FACE,{"disambiguationData":[OSD([subQ0])]})]});}
            fillet(context, id + "F14", {"entities" : qUnion([Q0, Q1, Q2, Q3, Q4, Q5, Q6, Q7, Q8, Q9, Q10, Q11, Q12, Q13, Q14, Q15, Q16, Q17, Q18, Q19, Q20, Q21, Q22, Q23]), "radius" : 5.08 * mm, "tangentPropagation" : true, "allowEdgeOverflow" : false});
        }
        {
            var Q0;
            Q0=qCreatedBy(makeId("Front.planeOp"),FACE);
            var sketch = newSketch(context, id + "F15", { "sketchPlane" : qUnion([Q0])});
            skLineSegment(sketch, "E51", {"start": v(0, 49.78) * mm, "end": v(12.7, 27.78) * mm});
            skLineSegment(sketch, "E52", {"start": v(12.7, 27.78) * mm, "end": v(-12.7, 27.78) * mm});
            skLineSegment(sketch, "E53", {"start": v(-12.7, 27.78) * mm, "end": v(0, 49.78) * mm});
            skSolve(sketch);
        }
        {
            var Q0;
            Q0=qCreatedBy(makeId("Right.planeOp"),FACE);
            var sketch = newSketch(context, id + "F16", { "sketchPlane" : qUnion([Q0])});
            skLineSegment(sketch, "E54", {"start": v(0, 47.96) * mm, "end": v(-12.7, 25.96) * mm});
            skLineSegment(sketch, "E55", {"start": v(-12.7, 25.96) * mm, "end": v(12.7, 25.96) * mm});
            skLineSegment(sketch, "E56", {"start": v(12.7, 25.96) * mm, "end": v(0, 47.96) * mm});
            skSolve(sketch);
        }
        {
            var Q0;
            Q0 = qSketchRegion(id + "F15", true);
            extrude(context, id + "F17", {"entities" : qUnion([Q0]), "endBound" : BoundingType.SYMMETRIC, "depth" : 25.4 * mm, "offsetDistance" : 25.4 * mm});
        }
        {
            var Q0;
            Q0 = qSketchRegion(id + "F16", true);
            extrude(context, id + "F18", {"entities" : qUnion([Q0]), "operationType" : NewBodyOperationType.ADD, "endBound" : BoundingType.SYMMETRIC, "depth" : 25.4 * mm, "offsetDistance" : 25.4 * mm});
        }
    });
